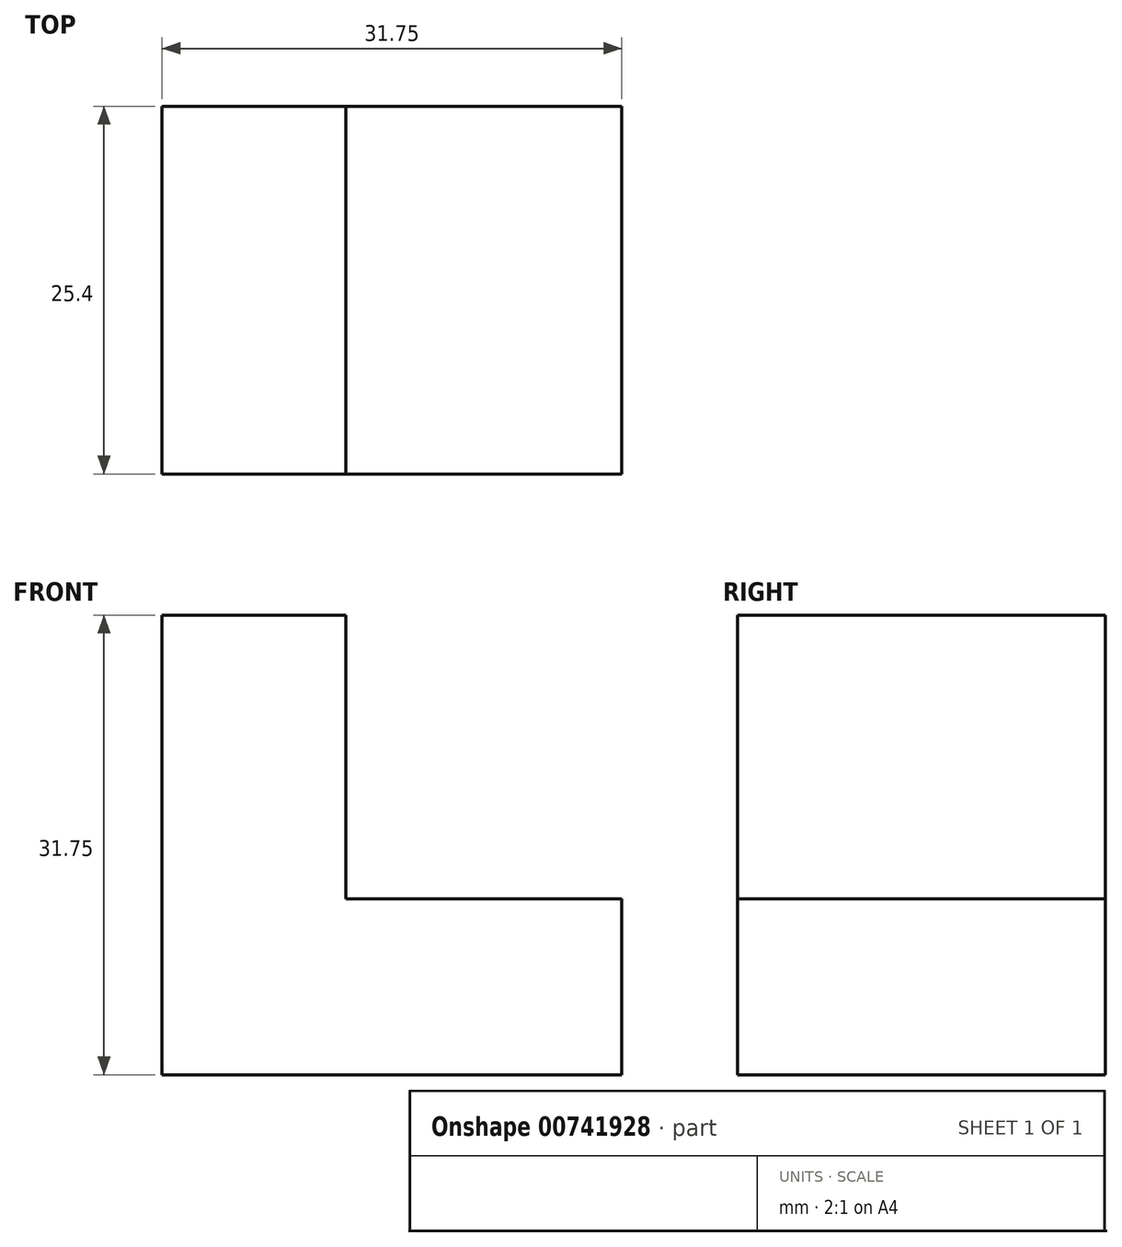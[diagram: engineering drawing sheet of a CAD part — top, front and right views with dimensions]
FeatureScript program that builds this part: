
annotation { "Feature Type Name" : "Feature", "Feature Type Description" : "" }
export const myFeature = defineFeature(function(context is Context, id is Id, definition is map)
    precondition{}
    {
        {
            var Q0;
            Q0=qCreatedBy(makeId("Front.planeOp"),FACE);
            var sketch = newSketch(context, id + "F0", { "sketchPlane" : qUnion([Q0])});
            skLineSegment(sketch, "E0", {"start": v(0, 31.75) * mm, "end": v(0, 0) * mm});
            skLineSegment(sketch, "E1", {"start": v(0, 0) * mm, "end": v(31.75, 0) * mm});
            skLineSegment(sketch, "E2", {"start": v(0, 31.75) * mm, "end": v(12.7, 31.75) * mm});
            skLineSegment(sketch, "E3", {"start": v(12.7, 31.75) * mm, "end": v(12.7, 12.16) * mm});
            skLineSegment(sketch, "E4", {"start": v(12.7, 12.16) * mm, "end": v(31.75, 12.16) * mm});
            skLineSegment(sketch, "E5", {"start": v(31.75, 12.16) * mm, "end": v(31.75, 0) * mm});
            skSolve(sketch);
        }
        {
            var Q0;
            Q0=makeQuery(id+"F0.imprint","IMPRINT",FACE,{"disambiguationData":[TD([[makeQuery(id+"F0.imprint","IMPRINT",EDGE,{"derivedFrom":sQuery(id+"F0.wireOp",EDGE,"E0")}),1.0]])]});
            extrude(context, id + "F1", {"entities" : qUnion([Q0]), "depth" : 25.4 * mm, "offsetDistance" : 25.4 * mm});
        }
    });
